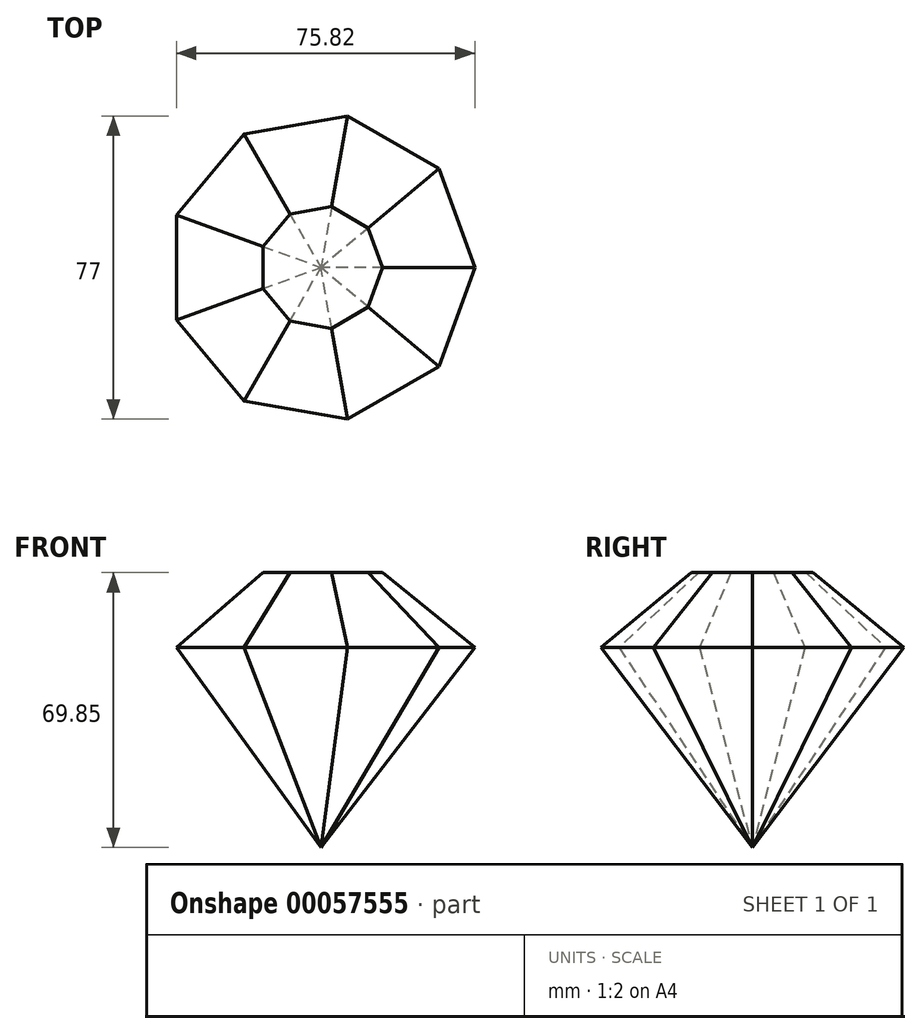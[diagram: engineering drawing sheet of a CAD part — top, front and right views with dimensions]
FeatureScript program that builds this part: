
annotation { "Feature Type Name" : "Feature", "Feature Type Description" : "" }
export const myFeature = defineFeature(function(context is Context, id is Id, definition is map)
    precondition{}
    {
        {
            var Q0;
            Q0=qCreatedBy(makeId("Top.planeOp"),FACE);
            var sketch = newSketch(context, id + "F0", { "sketchPlane" : qUnion([Q0])});
            skCircle(sketch, "E0.cCircle", {"center": v(0, 0) * mm, "radius": 36.73 * mm, "construction": true});
            skLineSegment(sketch, "E0.0", {"start": v(-36.73, -13.37) * mm, "end": v(-36.73, 13.37) * mm});
            skLineSegment(sketch, "E0.1", {"start": v(-36.73, 13.37) * mm, "end": v(-19.55, 33.85) * mm});
            skLineSegment(sketch, "E0.2", {"start": v(-19.55, 33.85) * mm, "end": v(6.79, 38.5) * mm});
            skLineSegment(sketch, "E0.3", {"start": v(6.79, 38.5) * mm, "end": v(29.95, 25.13) * mm});
            skLineSegment(sketch, "E0.4", {"start": v(29.95, 25.13) * mm, "end": v(39.1, 0) * mm});
            skLineSegment(sketch, "E0.5", {"start": v(39.1, 0) * mm, "end": v(29.95, -25.13) * mm});
            skLineSegment(sketch, "E0.6", {"start": v(29.95, -25.13) * mm, "end": v(6.79, -38.5) * mm});
            skLineSegment(sketch, "E0.7", {"start": v(6.79, -38.5) * mm, "end": v(-19.55, -33.85) * mm});
            skLineSegment(sketch, "E0.8", {"start": v(-19.55, -33.85) * mm, "end": v(-36.73, -13.37) * mm});
            skPoint(sketch, "E0.0.midPoint", {"position": v(-36.73, 0) * mm});
            skSolve(sketch);
        }
        {
            var Q0;
            Q0=qCreatedBy(makeId("Top.planeOp"),FACE);
            cPlane(context, id + "F1", {"entities" : qUnion([Q0]), "cplaneType" : CPlaneType.OFFSET, "offset" : 50.8 * mm, "oppositeDirection" : true, "width" : 152.4 * mm, "height" : 152.4 * mm});
        }
        {
            var Q0;
            Q0=qCreatedBy(id+"F1.planeOp",FACE);
            var sketch = newSketch(context, id + "F2", { "sketchPlane" : qUnion([Q0])});
            skCircle(sketch, "E1", {"center": v(0, 0) * mm, "radius": 0.43 * mm});
            skSolve(sketch);
        }
        {
            var Q0;
            Q0=makeQuery(id+"F0.imprint","IMPRINT",FACE,{"disambiguationData":[TD([[makeQuery(id+"F0.imprint","IMPRINT",EDGE,{"derivedFrom":sQuery(id+"F0.wireOp",EDGE,"E0.0")}),-1.0]])]});
            var Q1;
            Q1=sQuery(id+"F2.wireOp",VERTEX,"E1.center");
            loft(context, id + "F3", {"sheetProfilesArray" : [{ "sheetProfileEntities" : qUnion([Q0]) }, { "sheetProfileEntities" : qUnion([Q1]) }]});
        }
        {
            var Q0;
            Q0=qCreatedBy(makeId("Top.planeOp"),FACE);
            cPlane(context, id + "F4", {"entities" : qUnion([Q0]), "cplaneType" : CPlaneType.OFFSET, "offset" : 19.05 * mm, "width" : 152.4 * mm, "height" : 152.4 * mm});
        }
        {
            var Q0;
            Q0=qCreatedBy(id+"F4.planeOp",FACE);
            var sketch = newSketch(context, id + "F5", { "sketchPlane" : qUnion([Q0])});
            skLineSegment(sketch, "E2.0", {"start": v(-7.84, 13.58) * mm, "end": v(-14.73, 5.36) * mm});
            skLineSegment(sketch, "E2.1", {"start": v(2.72, 15.44) * mm, "end": v(-7.84, 13.58) * mm});
            skLineSegment(sketch, "E2.2", {"start": v(-14.73, 5.36) * mm, "end": v(-14.73, -5.36) * mm});
            skLineSegment(sketch, "E2.3", {"start": v(12.01, 10.08) * mm, "end": v(2.72, 15.44) * mm});
            skLineSegment(sketch, "E2.4", {"start": v(15.68, 0) * mm, "end": v(12.01, 10.08) * mm});
            skLineSegment(sketch, "E2.5", {"start": v(-14.73, -5.36) * mm, "end": v(-7.84, -13.58) * mm});
            skLineSegment(sketch, "E2.6", {"start": v(-7.84, -13.58) * mm, "end": v(2.72, -15.44) * mm});
            skLineSegment(sketch, "E2.7", {"start": v(2.72, -15.44) * mm, "end": v(12.01, -10.08) * mm});
            skLineSegment(sketch, "E2.8", {"start": v(12.01, -10.08) * mm, "end": v(15.68, 0) * mm});
            skSolve(sketch);
        }
        {
            var Q1;
            Q1=makeQuery(id+"F5.imprint","IMPRINT",FACE,{"disambiguationData":[TD([[makeQuery(id+"F5.imprint","IMPRINT",EDGE,{"derivedFrom":sQuery(id+"F5.wireOp",EDGE,"E2.0")}),1.0]])]});
            var Q2;
            Q2=makeQuery(id+"F0.imprint","IMPRINT",FACE,{"disambiguationData":[TD([[makeQuery(id+"F0.imprint","IMPRINT",EDGE,{"derivedFrom":sQuery(id+"F0.wireOp",EDGE,"E0.0")}),-1.0]])]});
            loft(context, id + "F6", {"operationType" : NewBodyOperationType.ADD, "sheetProfilesArray" : [{ "sheetProfileEntities" : qUnion([Q1]) }, { "sheetProfileEntities" : qUnion([Q2]) }]});
        }
    });
